# Revit family: FOR UPDATE_36731XXX_NEW
name_source: partatom
category: Plumbing Fixtures
revit_build: Autodesk Revit 2018 (Build: 20170223_1515(x64)
units: mm (PartAtom-declared; Revit-internal decimal feet)

## family parameters
Always vertical = No
Cut with Voids When Loaded = No
OmniClass Number = 23.31.17.00
OmniClass Title = Showers
Part Type = Normal
Room Calculation Point = No
Round Connector Dimension = Use Diameter
Shared = No
Work Plane-Based = Yes

## types (1)
- Default - please load Revit Family Type Catalog
    Always visible = Yes
    BIMobject category = Showers
    Connector Description = Water Inlet 12.7mm
    Default Elevation = 1219.2 mm  [stored 4 ft]
    Description = AXOR ShowerSolutions Wall outlet softsquare
    Design country = Germany
    Diameter = 13 mm
    EAN code = 4059625428597
    Edition number = 1
    GTIN code = https://4059625428597
    IFC Classification = Sanitary Terminal
    Manufacturer = AXOR
    Manufacturer country = Germany
    Manufacturer name = AXOR
    Material 1 = AXOR - Metal - 000 Chrome
    Material main = Plastic
    Material secondary = Chrome
    Model = 36731XXX
    OmniClass Code = 23-31 17 00
    OmniClass Description = Showers
    Product Guid = a25fc86a-88b2-47d0-b73b-f77762461d37
    Product SKU = 36731XXX
    Product data url = https://bimobject.com
    Product family = AXOR ShowerSolutions
    Product group = Wall outlet
    Product name = 36731XXX AXOR ShowerSolutions Wall outlet softsquare
    QR code = https://bimobject.com
    URL = https://www.axor-design.com
    Weight Net (Kg) = 90

note: [stored X ft] marks values corroborated as IEEE doubles in the binary element streams (Revit-internal decimal feet)

## geometry (parser evidence)
native form markers: Sweep x3
no freeform markers — native parametric forms only
